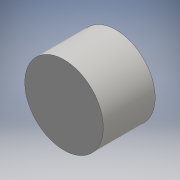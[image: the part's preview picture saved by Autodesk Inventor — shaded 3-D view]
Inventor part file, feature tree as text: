
AUTODESK INVENTOR PART (.ipt)
format: ipt  version: 2016 (Build 200138000, 138)  size: 87,040 bytes
history: native  units: mm
features: other x1, extrude x1, sketch x1
ambient origin geometry x8: Origin, YZ Plane, XZ Plane, XY Plane, X Axis, Y Axis, Z Axis, Center Point
bodies: Body1 (feature_tree)
feature tree (3):
  other  "ソリッド1"
  extrude  "押し出し1"  Depth=32.5mm
  sketch  "スケッチ1"
